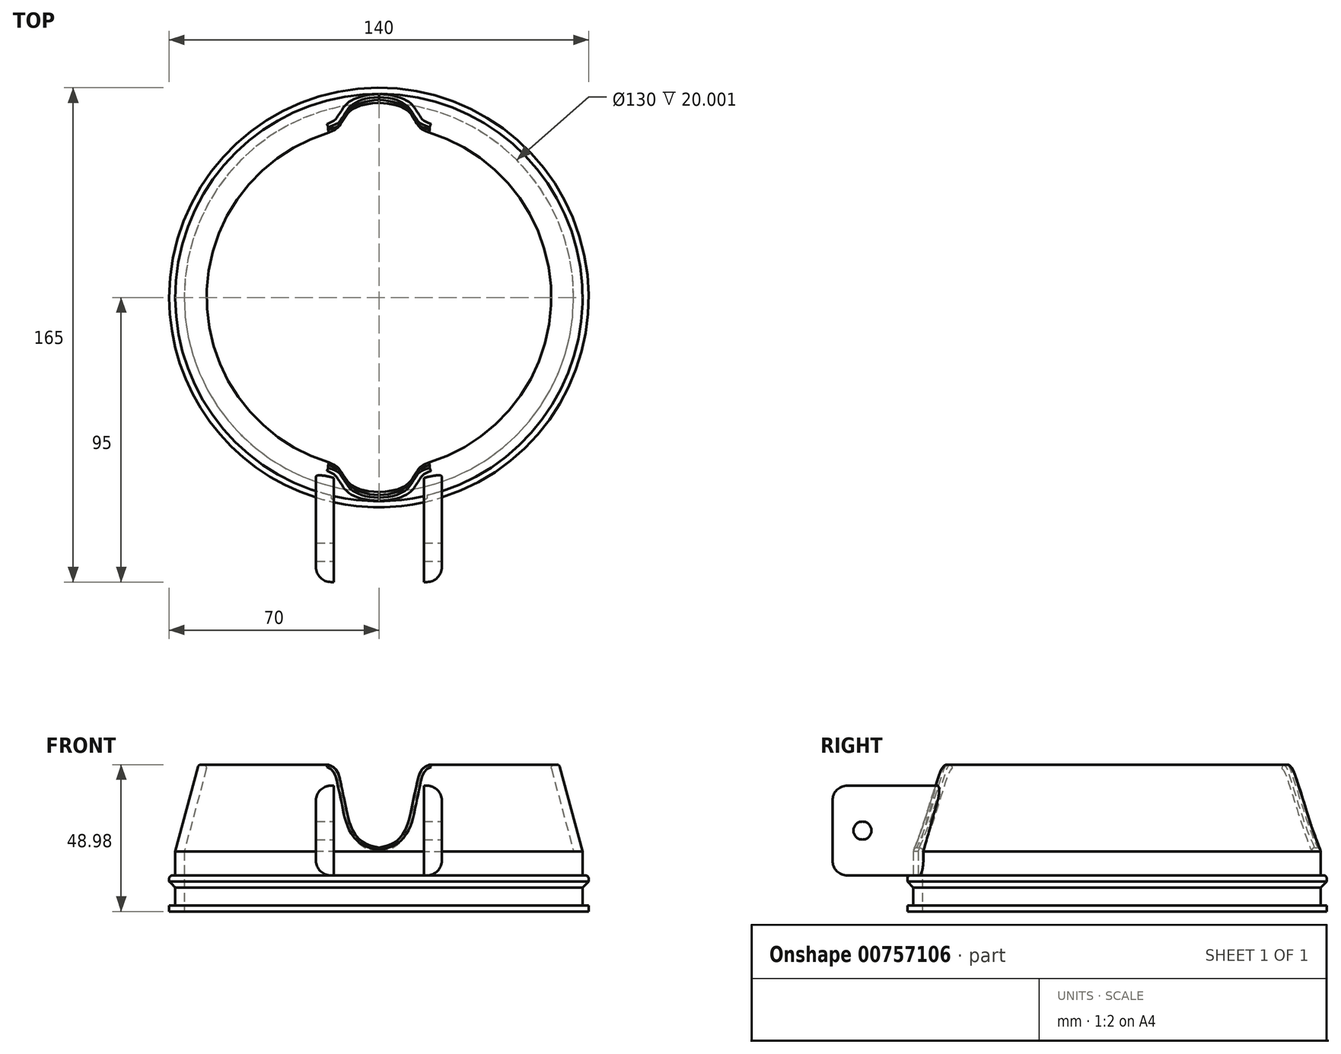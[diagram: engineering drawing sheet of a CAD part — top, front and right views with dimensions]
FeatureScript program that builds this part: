
annotation { "Feature Type Name" : "Feature", "Feature Type Description" : "" }
export const myFeature = defineFeature(function(context is Context, id is Id, definition is map)
    precondition{}
    {
        {
            var Q0;
            Q0=qCreatedBy(makeId("Front.planeOp"),FACE);
            var sketch = newSketch(context, id + "F0", { "sketchPlane" : qUnion([Q0])});
            skLineSegment(sketch, "E0.top", {"start": v(-68, 20) * mm, "end": v(-65, 20) * mm});
            skLineSegment(sketch, "E0.left", {"start": v(-68, 0) * mm, "end": v(-68, 20) * mm});
            skLineSegment(sketch, "E0.right", {"start": v(-65, 0) * mm, "end": v(-65, 20) * mm});
            skLineSegment(sketch, "E1", {"start": v(-68, 20) * mm, "end": v(-60.24, 48.98) * mm});
            skLineSegment(sketch, "E2", {"start": v(-57.24, 48.98) * mm, "end": v(-65, 20) * mm});
            skPoint(sketch, "E3.visualSharp", {"position": v(-68, 0) * mm});
            skPoint(sketch, "E4.visualSharp", {"position": v(-65, 0) * mm});
            skLineSegment(sketch, "E5", {"start": v(-68, 12) * mm, "end": v(-69, 12) * mm});
            skLineSegment(sketch, "E6", {"start": v(-70, 11) * mm, "end": v(-70, 10) * mm});
            skLineSegment(sketch, "E7", {"start": v(-70, 10) * mm, "end": v(-68, 8) * mm});
            skLineSegment(sketch, "E8", {"start": v(-68, 2) * mm, "end": v(-70, 2) * mm});
            skLineSegment(sketch, "E9", {"start": v(-70, 2) * mm, "end": v(-70, 0) * mm});
            skLineSegment(sketch, "E10", {"start": v(-70, 0) * mm, "end": v(-68, 0) * mm});
            skPoint(sketch, "E11.visualSharp", {"position": v(-70, 12) * mm});
            skArc(sketch, "E11.filletArc", {"start": v(-69, 12) * mm, "mid": v(-69.7, 11.7) * mm, "end": v(-70, 11) * mm});
            skLineSegment(sketch, "E12", {"start": v(0, 0) * mm, "end": v(0, 37.2) * mm, "construction": true});
            skLineSegment(sketch, "E13", {"start": v(-60.24, 48.98) * mm, "end": v(-57.24, 48.98) * mm});
            skLineSegment(sketch, "E14", {"start": v(-68, 0) * mm, "end": v(-65, 0) * mm});
            skSolve(sketch);
        }
        {
            var Q0;
            Q0=makeQuery(id+"F0.imprint","IMPRINT",FACE,{"disambiguationData":[TD([[makeQuery(id+"F0.imprint","IMPRINT",EDGE,{"derivedFrom":sQuery(id+"F0.wireOp",EDGE,"E0.bottom")}),1.0]])]});
            var Q1;
            {var subQ0=sQuery(id+"F0.wireOp",EDGE,"E0.top");Q1=makeQuery(id+"F0.imprint","IMPRINT",FACE,{"disambiguationData":[TD([[makeQuery(id+"F0.imprint","IMPRINT",EDGE,{"derivedFrom":subQ0}),1.0]])]});}
            var Q2;
            Q2=makeQuery(id+"F0.imprint","IMPRINT",FACE,{"disambiguationData":[TD([[makeQuery(id+"F0.imprint","IMPRINT",EDGE,{"derivedFrom":sQuery(id+"F0.wireOp",EDGE,"ip61VsO4-G4QX-MuCQ-3TD0-dqhbcXr0CBei")}),1.0]])]});
            var Q3;
            {var subQ1=sQuery(id+"F0.wireOp",EDGE,"E5");Q3=makeQuery(id+"F0.imprint","IMPRINT",FACE,{"disambiguationData":[TD([[makeQuery(id+"F0.imprint","IMPRINT",EDGE,{"derivedFrom":subQ1}),1.0]])]});}
            var Q4;
            {var subQ0=sQuery(id+"F0.wireOp",EDGE,"E8");Q4=makeQuery(id+"F0.imprint","IMPRINT",FACE,{"disambiguationData":[TD([[makeQuery(id+"F0.imprint","IMPRINT",EDGE,{"derivedFrom":subQ0}),1.0]])]});}
            var Q5;
            {var subQ5=sQuery(id+"F0.wireOp",EDGE,"E0.top");Q5=makeQuery(id+"F0.imprint","IMPRINT",FACE,{"disambiguationData":[TD([[makeQuery(id+"F0.imprint","IMPRINT",EDGE,{"derivedFrom":subQ5}),-1.0]])]});}
            var Q6;
            Q6=sQuery(id+"F0.wireOp",EDGE,"E12");
            revolve(context, id + "F1", {"surfaceOperationType" : NewSurfaceOperationType.NEW, "entities" : qUnion([Q0, Q1, Q2, Q3, Q4, Q5]), "axis" : qUnion([Q6]), "revolveType" : RevolveType.FULL});
        }
        {
            var Q0;
            Q0=qCreatedBy(makeId("Front.planeOp"),FACE);
            var sketch = newSketch(context, id + "F2", { "sketchPlane" : qUnion([Q0])});
            skFitSpline(sketch, "E15", {"points": [v(21.47, 49.66) * mm, v(17.18, 49.05) * mm, v(14.22, 47.2) * mm, v(12.69, 42.71) * mm, v(11.26, 35.97) * mm, v(9.52, 28.93) * mm, v(5.64, 23.3) * mm, v(0, 21.26) * mm], "startDerivative": vector(-35.25, -2.77) * mm, "endDerivative": vector(-40.6, -8.65) * mm});
            skFitSpline(sketch, "E16.MirrorCS", {"points": [v(-21.47, 49.66) * mm, v(-17.18, 49.05) * mm, v(-14.22, 47.2) * mm, v(-12.69, 42.71) * mm, v(-11.26, 35.97) * mm, v(-9.52, 28.93) * mm, v(-5.64, 23.3) * mm, v(0, 21.26) * mm], "startDerivative": vector(35.25, -2.77) * mm, "endDerivative": vector(40.6, -8.65) * mm});
            skLineSegment(sketch, "E17", {"start": v(21.47, 49.66) * mm, "end": v(21.47, 54.46) * mm});
            skLineSegment(sketch, "E18", {"start": v(21.47, 54.46) * mm, "end": v(-21.12, 54.46) * mm});
            skLineSegment(sketch, "E19", {"start": v(-21.12, 54.46) * mm, "end": v(-21.47, 49.66) * mm});
            skSolve(sketch);
        }
        {
            var Q0;
            Q0 = qSketchRegion(id + "F2", true);
            extrude(context, id + "F3", {"entities" : qUnion([Q0]), "operationType" : NewBodyOperationType.REMOVE, "endBound" : BoundingType.SYMMETRIC, "depth" : 200 * mm, "offsetDistance" : 25 * mm});
        }
        {
            var Q0;
            Q0=qCreatedBy(makeId("Front.planeOp"),FACE);
            cPlane(context, id + "F4", {"entities" : qUnion([Q0]), "cplaneType" : CPlaneType.OFFSET, "offset" : 95 * mm, "width" : 150 * mm, "height" : 150 * mm});
        }
        {
            var Q0;
            Q0=qCreatedBy(id+"F4.planeOp",FACE);
            var sketch = newSketch(context, id + "F5", { "sketchPlane" : qUnion([Q0])});
            skLineSegment(sketch, "E20.bottom", {"start": v(-21, 42) * mm, "end": v(-15, 42) * mm});
            skLineSegment(sketch, "E20.top", {"start": v(-21, 12) * mm, "end": v(-15, 12) * mm});
            skLineSegment(sketch, "E20.left", {"start": v(-21, 42) * mm, "end": v(-21, 12) * mm});
            skLineSegment(sketch, "E20.right", {"start": v(-15, 42) * mm, "end": v(-15, 12) * mm});
            skLineSegment(sketch, "E21.MirrorCS", {"start": v(15, 42) * mm, "end": v(15, 12) * mm});
            skLineSegment(sketch, "E22.MirrorCS", {"start": v(21, 42) * mm, "end": v(15, 42) * mm});
            skLineSegment(sketch, "E23.MirrorCS", {"start": v(21, 12) * mm, "end": v(15, 12) * mm});
            skLineSegment(sketch, "E24.MirrorCS", {"start": v(21, 42) * mm, "end": v(21, 12) * mm});
            skSolve(sketch);
        }
        {
            var Q0;
            Q0 = qSketchRegion(id + "F5", true);
            extrude(context, id + "F6", {"entities" : qUnion([Q0]), "operationType" : NewBodyOperationType.ADD, "endBound" : BoundingType.UP_TO_NEXT, "oppositeDirection" : true, "depth" : 25 * mm, "offsetDistance" : 25 * mm});
        }
        {
            var Q0;
            Q0=makeQuery(id+"F6.opExtrude","CAP_EDGE",EDGE,{"disambiguationData":[OSD([sQuery(id+"F5.wireOp",EDGE,"E20.bottom")])],"isStart":true});
            var Q1;
            Q1=makeQuery(id+"F6.opExtrude","CAP_EDGE",EDGE,{"disambiguationData":[OSD([sQuery(id+"F5.wireOp",EDGE,"E20.top")])],"isStart":true});
            var Q2;
            Q2=makeQuery(id+"F6.opExtrude","CAP_EDGE",EDGE,{"disambiguationData":[OSD([sQuery(id+"F5.wireOp",EDGE,"E22.MirrorCS")])],"isStart":true});
            var Q3;
            Q3=makeQuery(id+"F6.opExtrude","CAP_EDGE",EDGE,{"disambiguationData":[OSD([sQuery(id+"F5.wireOp",EDGE,"E23.MirrorCS")])],"isStart":true});
            fillet(context, id + "F7", {"entities" : qUnion([Q0, Q1, Q2, Q3]), "radius" : 5 * mm, "tangentPropagation" : true, "allowEdgeOverflow" : false});
        }
        {
            var Q0;
            Q0=makeQuery(id+"F6.opExtrude","SWEPT_FACE",FACE,{"disambiguationData":[OSD([sQuery(id+"F5.wireOp",EDGE,"E24.MirrorCS")])]});
            var sketch = newSketch(context, id + "F8", { "sketchPlane" : qUnion([Q0])});
            skCircle(sketch, "E25", {"center": v(-85, 27) * mm, "radius": 3 * mm});
            skPoint(sketch, "E25.centerSnap0", {"position": v(-95, 27) * mm});
            skSolve(sketch);
        }
        {
            var Q0;
            Q0=makeQuery(id+"F8.imprint","IMPRINT",FACE,{"disambiguationData":[TD([[makeQuery(id+"F8.imprint","IMPRINT",EDGE,{"derivedFrom":sQuery(id+"F8.wireOp",EDGE,"E25")}),1.0]])]});
            extrude(context, id + "F9", {"entities" : qUnion([Q0]), "operationType" : NewBodyOperationType.REMOVE, "endBound" : BoundingType.THROUGH_ALL, "oppositeDirection" : true, "depth" : 25 * mm, "offsetDistance" : 25 * mm});
        }
        {
            var Q0;
            Q0=makeQuery(id+"F6.opExtrude","CAP_EDGE",EDGE,{"disambiguationData":[OSD([sQuery(id+"F5.wireOp",EDGE,"E20.left")])],"isStart":true});
            var Q1;
            Q1=makeQuery(id+"F6.opExtrude","CAP_EDGE",EDGE,{"disambiguationData":[OSD([sQuery(id+"F5.wireOp",EDGE,"E24.MirrorCS")])],"isStart":true});
            fillet(context, id + "F10", {"entities" : qUnion([Q0, Q1]), "radius" : 5 * mm, "tangentPropagation" : true, "allowEdgeOverflow" : false});
        }
        {
            var Q0;
            {var subQ0=sQuery(id+"F0.wireOp",EDGE,"E2");var subQ2=sQuery(id+"F0.wireOp",EDGE,"E13");var subQ4=makeQuery(id+"F3.opExtrude","SWEPT_FACE",FACE,{"disambiguationData":[OSD([sQuery(id+"F2.wireOp",EDGE,"E16.MirrorCS")])]});Q0=makeQuery(id+"Fq1PH19bnDTYdRj_1.1.F3.boolean.opBoolean","SPLIT",EDGE,{"disambiguationData":[TD([makeQuery(id+"F3.boolean.opBoolean","COPY",FACE,{"disambiguationData":[OD(0.0)],"derivedFrom":subQ4})])],"derivedFrom":makeQuery(id+"F3.boolean.opBoolean","SPLIT",EDGE,{"disambiguationData":[TD([subQ4])],"derivedFrom":makeQuery(id+"F1.opRevolve","SWEPT_EDGE",EDGE,{"disambiguationData":[OSD([subQ0,subQ2])]})})});}
            var Q1;
            Q1=makeQuery(id+"F3.boolean.opBoolean","INTERSECT",EDGE,{"disambiguationData":[OD(0.0)],"derivedFrom":[makeQuery(id+"F1.opRevolve","SWEPT_FACE",FACE,{"disambiguationData":[OSD([sQuery(id+"F0.wireOp",EDGE,"E2")])]}),makeQuery(id+"F3.opExtrude","SWEPT_FACE",FACE,{"disambiguationData":[OSD([sQuery(id+"F2.wireOp",EDGE,"E16.MirrorCS")])]})]});
            var Q2;
            Q2=makeQuery(id+"F3.boolean.opBoolean","INTERSECT",EDGE,{"disambiguationData":[OD(0.0)],"derivedFrom":[makeQuery(id+"F1.opRevolve","SWEPT_FACE",FACE,{"disambiguationData":[OSD([sQuery(id+"F0.wireOp",EDGE,"E2")])]}),makeQuery(id+"F3.opExtrude","SWEPT_FACE",FACE,{"disambiguationData":[OSD([sQuery(id+"F2.wireOp",EDGE,"E15")])]})]});
            var Q3;
            {var subQ0=sQuery(id+"F0.wireOp",EDGE,"E2");var subQ2=sQuery(id+"F2.wireOp",EDGE,"E15");var subQ3=makeQuery(id+"F3.opExtrude","SWEPT_FACE",FACE,{"disambiguationData":[OSD([subQ2])]});var subQ4=makeQuery(id+"F3.boolean.opBoolean","COPY",FACE,{"disambiguationData":[OD(0.0)],"derivedFrom":subQ3});var subQ5=sQuery(id+"F0.wireOp",EDGE,"E13");Q3=makeQuery(id+"Fq1PH19bnDTYdRj_1.3.F3.boolean.opBoolean","SPLIT",EDGE,{"disambiguationData":[TD([subQ4])],"derivedFrom":makeQuery(id+"Fq1PH19bnDTYdRj_1.2.F3.boolean.opBoolean","SPLIT",EDGE,{"disambiguationData":[TD([subQ4])],"derivedFrom":makeQuery(id+"Fq1PH19bnDTYdRj_1.1.F3.boolean.opBoolean","SPLIT",EDGE,{"disambiguationData":[TD([subQ4])],"derivedFrom":makeQuery(id+"F3.boolean.opBoolean","SPLIT",EDGE,{"disambiguationData":[TD([subQ3])],"derivedFrom":makeQuery(id+"F1.opRevolve","SWEPT_EDGE",EDGE,{"disambiguationData":[OSD([subQ0,subQ5])]})})})})});}
            var Q4;
            Q4=makeQuery(id+"Fq1PH19bnDTYdRj_1.3.F3.boolean.opBoolean","INTERSECT",EDGE,{"disambiguationData":[OD(1.0)],"derivedFrom":[makeQuery(id+"F1.opRevolve","SWEPT_FACE",FACE,{"disambiguationData":[OSD([sQuery(id+"F0.wireOp",EDGE,"E2")])]}),makeQuery(id+"Fq1PH19bnDTYdRj_1.3.F3.opExtrude","SWEPT_FACE",FACE,{"disambiguationData":[OSD([sQuery(id+"F2.wireOp",EDGE,"E15")])]})]});
            var Q5;
            Q5=makeQuery(id+"Fq1PH19bnDTYdRj_1.3.F3.boolean.opBoolean","INTERSECT",EDGE,{"disambiguationData":[OD(1.0)],"derivedFrom":[makeQuery(id+"F1.opRevolve","SWEPT_FACE",FACE,{"disambiguationData":[OSD([sQuery(id+"F0.wireOp",EDGE,"E2")])]}),makeQuery(id+"Fq1PH19bnDTYdRj_1.3.F3.opExtrude","SWEPT_FACE",FACE,{"disambiguationData":[OSD([sQuery(id+"F2.wireOp",EDGE,"E16.MirrorCS")])]})]});
            var Q6;
            {var subQ0=sQuery(id+"F0.wireOp",EDGE,"E2");var subQ2=sQuery(id+"F0.wireOp",EDGE,"E13");var subQ4=sQuery(id+"F2.wireOp",EDGE,"E15");var subQ5=makeQuery(id+"Fq1PH19bnDTYdRj_1.2.F3.opExtrude","SWEPT_FACE",FACE,{"disambiguationData":[OSD([subQ4])]});var subQ6=makeQuery(id+"F3.opExtrude","SWEPT_FACE",FACE,{"disambiguationData":[OSD([subQ4])]});var subQ7=makeQuery(id+"F3.boolean.opBoolean","COPY",FACE,{"disambiguationData":[OD(0.0)],"derivedFrom":subQ6});Q6=makeQuery(id+"Fq1PH19bnDTYdRj_1.3.F3.boolean.opBoolean","SPLIT",EDGE,{"disambiguationData":[TD([makeQuery(id+"Fq1PH19bnDTYdRj_1.2.F3.boolean.opBoolean","COPY",FACE,{"disambiguationData":[OD(1.0)],"derivedFrom":subQ5})])],"derivedFrom":makeQuery(id+"Fq1PH19bnDTYdRj_1.2.F3.boolean.opBoolean","SPLIT",EDGE,{"disambiguationData":[TD([subQ7])],"derivedFrom":makeQuery(id+"Fq1PH19bnDTYdRj_1.1.F3.boolean.opBoolean","SPLIT",EDGE,{"disambiguationData":[TD([subQ7])],"derivedFrom":makeQuery(id+"F3.boolean.opBoolean","SPLIT",EDGE,{"disambiguationData":[TD([subQ6])],"derivedFrom":makeQuery(id+"F1.opRevolve","SWEPT_EDGE",EDGE,{"disambiguationData":[OSD([subQ0,subQ2])]})})})})});}
            var Q7;
            Q7=makeQuery(id+"Fq1PH19bnDTYdRj_1.2.F3.boolean.opBoolean","INTERSECT",EDGE,{"disambiguationData":[OD(1.0)],"derivedFrom":[makeQuery(id+"F1.opRevolve","SWEPT_FACE",FACE,{"disambiguationData":[OSD([sQuery(id+"F0.wireOp",EDGE,"E2")])]}),makeQuery(id+"Fq1PH19bnDTYdRj_1.2.F3.opExtrude","SWEPT_FACE",FACE,{"disambiguationData":[OSD([sQuery(id+"F2.wireOp",EDGE,"E15")])]})]});
            var Q8;
            Q8=makeQuery(id+"Fq1PH19bnDTYdRj_1.2.F3.boolean.opBoolean","INTERSECT",EDGE,{"disambiguationData":[OD(1.0)],"derivedFrom":[makeQuery(id+"F1.opRevolve","SWEPT_FACE",FACE,{"disambiguationData":[OSD([sQuery(id+"F0.wireOp",EDGE,"E2")])]}),makeQuery(id+"Fq1PH19bnDTYdRj_1.2.F3.opExtrude","SWEPT_FACE",FACE,{"disambiguationData":[OSD([sQuery(id+"F2.wireOp",EDGE,"E16.MirrorCS")])]})]});
            var Q9;
            {var subQ0=sQuery(id+"F0.wireOp",EDGE,"E2");var subQ2=sQuery(id+"F2.wireOp",EDGE,"E15");var subQ3=makeQuery(id+"Fq1PH19bnDTYdRj_1.1.F3.opExtrude","SWEPT_FACE",FACE,{"disambiguationData":[OSD([subQ2])]});var subQ4=sQuery(id+"F0.wireOp",EDGE,"E13");var subQ6=makeQuery(id+"F3.opExtrude","SWEPT_FACE",FACE,{"disambiguationData":[OSD([subQ2])]});Q9=makeQuery(id+"Fq1PH19bnDTYdRj_1.2.F3.boolean.opBoolean","SPLIT",EDGE,{"disambiguationData":[TD([makeQuery(id+"Fq1PH19bnDTYdRj_1.1.F3.boolean.opBoolean","COPY",FACE,{"disambiguationData":[OD(1.0)],"derivedFrom":subQ3})])],"derivedFrom":makeQuery(id+"Fq1PH19bnDTYdRj_1.1.F3.boolean.opBoolean","SPLIT",EDGE,{"disambiguationData":[TD([makeQuery(id+"F3.boolean.opBoolean","COPY",FACE,{"disambiguationData":[OD(0.0)],"derivedFrom":subQ6})])],"derivedFrom":makeQuery(id+"F3.boolean.opBoolean","SPLIT",EDGE,{"disambiguationData":[TD([subQ6])],"derivedFrom":makeQuery(id+"F1.opRevolve","SWEPT_EDGE",EDGE,{"disambiguationData":[OSD([subQ0,subQ4])]})})})});}
            var Q10;
            Q10=makeQuery(id+"Fq1PH19bnDTYdRj_1.1.F3.boolean.opBoolean","INTERSECT",EDGE,{"disambiguationData":[OD(1.0)],"derivedFrom":[makeQuery(id+"F1.opRevolve","SWEPT_FACE",FACE,{"disambiguationData":[OSD([sQuery(id+"F0.wireOp",EDGE,"E2")])]}),makeQuery(id+"Fq1PH19bnDTYdRj_1.1.F3.opExtrude","SWEPT_FACE",FACE,{"disambiguationData":[OSD([sQuery(id+"F2.wireOp",EDGE,"E15")])]})]});
            var Q11;
            Q11=makeQuery(id+"Fq1PH19bnDTYdRj_1.1.F3.boolean.opBoolean","INTERSECT",EDGE,{"disambiguationData":[OD(1.0)],"derivedFrom":[makeQuery(id+"F1.opRevolve","SWEPT_FACE",FACE,{"disambiguationData":[OSD([sQuery(id+"F0.wireOp",EDGE,"E2")])]}),makeQuery(id+"Fq1PH19bnDTYdRj_1.1.F3.opExtrude","SWEPT_FACE",FACE,{"disambiguationData":[OSD([sQuery(id+"F2.wireOp",EDGE,"E16.MirrorCS")])]})]});
            var Q12;
            {var subQ0=sQuery(id+"F0.wireOp",EDGE,"E2");var subQ2=sQuery(id+"F0.wireOp",EDGE,"E13");var subQ4=makeQuery(id+"F3.opExtrude","SWEPT_FACE",FACE,{"disambiguationData":[OSD([sQuery(id+"F2.wireOp",EDGE,"E15")])]});Q12=makeQuery(id+"Fq1PH19bnDTYdRj_1.1.F3.boolean.opBoolean","SPLIT",EDGE,{"disambiguationData":[TD([makeQuery(id+"F3.boolean.opBoolean","COPY",FACE,{"disambiguationData":[OD(1.0)],"derivedFrom":subQ4})])],"derivedFrom":makeQuery(id+"F3.boolean.opBoolean","SPLIT",EDGE,{"disambiguationData":[TD([subQ4])],"derivedFrom":makeQuery(id+"F1.opRevolve","SWEPT_EDGE",EDGE,{"disambiguationData":[OSD([subQ0,subQ2])]})})});}
            var Q13;
            Q13=makeQuery(id+"F3.boolean.opBoolean","INTERSECT",EDGE,{"disambiguationData":[OD(1.0)],"derivedFrom":[makeQuery(id+"F1.opRevolve","SWEPT_FACE",FACE,{"disambiguationData":[OSD([sQuery(id+"F0.wireOp",EDGE,"E2")])]}),makeQuery(id+"F3.opExtrude","SWEPT_FACE",FACE,{"disambiguationData":[OSD([sQuery(id+"F2.wireOp",EDGE,"E15")])]})]});
            var Q14;
            Q14=makeQuery(id+"F3.boolean.opBoolean","INTERSECT",EDGE,{"disambiguationData":[OD(1.0)],"derivedFrom":[makeQuery(id+"F1.opRevolve","SWEPT_FACE",FACE,{"disambiguationData":[OSD([sQuery(id+"F0.wireOp",EDGE,"E2")])]}),makeQuery(id+"F3.opExtrude","SWEPT_FACE",FACE,{"disambiguationData":[OSD([sQuery(id+"F2.wireOp",EDGE,"E16.MirrorCS")])]})]});
            var Q15;
            {var subQ0=sQuery(id+"F0.wireOp",EDGE,"E2");var subQ2=sQuery(id+"F0.wireOp",EDGE,"E13");var subQ4=sQuery(id+"F2.wireOp",EDGE,"E16.MirrorCS");var subQ5=makeQuery(id+"F3.opExtrude","SWEPT_FACE",FACE,{"disambiguationData":[OSD([subQ4])]});var subQ6=makeQuery(id+"F3.boolean.opBoolean","COPY",FACE,{"disambiguationData":[OD(1.0)],"derivedFrom":subQ5});Q15=makeQuery(id+"Fq1PH19bnDTYdRj_1.3.F3.boolean.opBoolean","SPLIT",EDGE,{"disambiguationData":[TD([subQ6])],"derivedFrom":makeQuery(id+"Fq1PH19bnDTYdRj_1.2.F3.boolean.opBoolean","SPLIT",EDGE,{"disambiguationData":[TD([subQ6])],"derivedFrom":makeQuery(id+"Fq1PH19bnDTYdRj_1.1.F3.boolean.opBoolean","SPLIT",EDGE,{"disambiguationData":[TD([subQ6])],"derivedFrom":makeQuery(id+"F3.boolean.opBoolean","SPLIT",EDGE,{"disambiguationData":[TD([subQ5])],"derivedFrom":makeQuery(id+"F1.opRevolve","SWEPT_EDGE",EDGE,{"disambiguationData":[OSD([subQ0,subQ2])]})})})})});}
            var Q16;
            Q16=makeQuery(id+"Fq1PH19bnDTYdRj_1.3.F3.boolean.opBoolean","INTERSECT",EDGE,{"disambiguationData":[OD(0.0)],"derivedFrom":[makeQuery(id+"F1.opRevolve","SWEPT_FACE",FACE,{"disambiguationData":[OSD([sQuery(id+"F0.wireOp",EDGE,"E2")])]}),makeQuery(id+"Fq1PH19bnDTYdRj_1.3.F3.opExtrude","SWEPT_FACE",FACE,{"disambiguationData":[OSD([sQuery(id+"F2.wireOp",EDGE,"E16.MirrorCS")])]})]});
            var Q17;
            Q17=makeQuery(id+"Fq1PH19bnDTYdRj_1.3.F3.boolean.opBoolean","INTERSECT",EDGE,{"disambiguationData":[OD(0.0)],"derivedFrom":[makeQuery(id+"F1.opRevolve","SWEPT_FACE",FACE,{"disambiguationData":[OSD([sQuery(id+"F0.wireOp",EDGE,"E2")])]}),makeQuery(id+"Fq1PH19bnDTYdRj_1.3.F3.opExtrude","SWEPT_FACE",FACE,{"disambiguationData":[OSD([sQuery(id+"F2.wireOp",EDGE,"E15")])]})]});
            var Q18;
            {var subQ0=sQuery(id+"F0.wireOp",EDGE,"E2");var subQ2=sQuery(id+"F0.wireOp",EDGE,"E13");var subQ4=sQuery(id+"F2.wireOp",EDGE,"E16.MirrorCS");var subQ5=makeQuery(id+"Fq1PH19bnDTYdRj_1.2.F3.opExtrude","SWEPT_FACE",FACE,{"disambiguationData":[OSD([subQ4])]});var subQ6=makeQuery(id+"F3.opExtrude","SWEPT_FACE",FACE,{"disambiguationData":[OSD([subQ4])]});var subQ7=makeQuery(id+"F3.boolean.opBoolean","COPY",FACE,{"disambiguationData":[OD(1.0)],"derivedFrom":subQ6});Q18=makeQuery(id+"Fq1PH19bnDTYdRj_1.3.F3.boolean.opBoolean","SPLIT",EDGE,{"disambiguationData":[TD([makeQuery(id+"Fq1PH19bnDTYdRj_1.2.F3.boolean.opBoolean","COPY",FACE,{"disambiguationData":[OD(0.0)],"derivedFrom":subQ5})])],"derivedFrom":makeQuery(id+"Fq1PH19bnDTYdRj_1.2.F3.boolean.opBoolean","SPLIT",EDGE,{"disambiguationData":[TD([subQ7])],"derivedFrom":makeQuery(id+"Fq1PH19bnDTYdRj_1.1.F3.boolean.opBoolean","SPLIT",EDGE,{"disambiguationData":[TD([subQ7])],"derivedFrom":makeQuery(id+"F3.boolean.opBoolean","SPLIT",EDGE,{"disambiguationData":[TD([subQ6])],"derivedFrom":makeQuery(id+"F1.opRevolve","SWEPT_EDGE",EDGE,{"disambiguationData":[OSD([subQ0,subQ2])]})})})})});}
            var Q19;
            Q19=makeQuery(id+"Fq1PH19bnDTYdRj_1.2.F3.boolean.opBoolean","INTERSECT",EDGE,{"disambiguationData":[OD(0.0)],"derivedFrom":[makeQuery(id+"F1.opRevolve","SWEPT_FACE",FACE,{"disambiguationData":[OSD([sQuery(id+"F0.wireOp",EDGE,"E2")])]}),makeQuery(id+"Fq1PH19bnDTYdRj_1.2.F3.opExtrude","SWEPT_FACE",FACE,{"disambiguationData":[OSD([sQuery(id+"F2.wireOp",EDGE,"E16.MirrorCS")])]})]});
            var Q20;
            Q20=makeQuery(id+"Fq1PH19bnDTYdRj_1.2.F3.boolean.opBoolean","INTERSECT",EDGE,{"disambiguationData":[OD(0.0)],"derivedFrom":[makeQuery(id+"F1.opRevolve","SWEPT_FACE",FACE,{"disambiguationData":[OSD([sQuery(id+"F0.wireOp",EDGE,"E2")])]}),makeQuery(id+"Fq1PH19bnDTYdRj_1.2.F3.opExtrude","SWEPT_FACE",FACE,{"disambiguationData":[OSD([sQuery(id+"F2.wireOp",EDGE,"E15")])]})]});
            var Q21;
            {var subQ0=sQuery(id+"F0.wireOp",EDGE,"E2");var subQ2=sQuery(id+"F0.wireOp",EDGE,"E13");var subQ4=sQuery(id+"F2.wireOp",EDGE,"E16.MirrorCS");var subQ5=makeQuery(id+"Fq1PH19bnDTYdRj_1.1.F3.opExtrude","SWEPT_FACE",FACE,{"disambiguationData":[OSD([subQ4])]});var subQ6=makeQuery(id+"F3.opExtrude","SWEPT_FACE",FACE,{"disambiguationData":[OSD([subQ4])]});Q21=makeQuery(id+"Fq1PH19bnDTYdRj_1.2.F3.boolean.opBoolean","SPLIT",EDGE,{"disambiguationData":[TD([makeQuery(id+"Fq1PH19bnDTYdRj_1.1.F3.boolean.opBoolean","COPY",FACE,{"disambiguationData":[OD(0.0)],"derivedFrom":subQ5})])],"derivedFrom":makeQuery(id+"Fq1PH19bnDTYdRj_1.1.F3.boolean.opBoolean","SPLIT",EDGE,{"disambiguationData":[TD([makeQuery(id+"F3.boolean.opBoolean","COPY",FACE,{"disambiguationData":[OD(1.0)],"derivedFrom":subQ6})])],"derivedFrom":makeQuery(id+"F3.boolean.opBoolean","SPLIT",EDGE,{"disambiguationData":[TD([subQ6])],"derivedFrom":makeQuery(id+"F1.opRevolve","SWEPT_EDGE",EDGE,{"disambiguationData":[OSD([subQ0,subQ2])]})})})});}
            var Q22;
            Q22=makeQuery(id+"Fq1PH19bnDTYdRj_1.1.F3.boolean.opBoolean","INTERSECT",EDGE,{"disambiguationData":[OD(0.0)],"derivedFrom":[makeQuery(id+"F1.opRevolve","SWEPT_FACE",FACE,{"disambiguationData":[OSD([sQuery(id+"F0.wireOp",EDGE,"E2")])]}),makeQuery(id+"Fq1PH19bnDTYdRj_1.1.F3.opExtrude","SWEPT_FACE",FACE,{"disambiguationData":[OSD([sQuery(id+"F2.wireOp",EDGE,"E16.MirrorCS")])]})]});
            var Q23;
            Q23=makeQuery(id+"Fq1PH19bnDTYdRj_1.1.F3.boolean.opBoolean","INTERSECT",EDGE,{"disambiguationData":[OD(0.0)],"derivedFrom":[makeQuery(id+"F1.opRevolve","SWEPT_FACE",FACE,{"disambiguationData":[OSD([sQuery(id+"F0.wireOp",EDGE,"E2")])]}),makeQuery(id+"Fq1PH19bnDTYdRj_1.1.F3.opExtrude","SWEPT_FACE",FACE,{"disambiguationData":[OSD([sQuery(id+"F2.wireOp",EDGE,"E15")])]})]});
            fillet(context, id + "F11", {"entities" : qUnion([Q0, Q1, Q2, Q3, Q4, Q5, Q6, Q7, Q8, Q9, Q10, Q11, Q12, Q13, Q14, Q15, Q16, Q17, Q18, Q19, Q20, Q21, Q22, Q23]), "radius" : 1 * mm, "tangentPropagation" : true, "allowEdgeOverflow" : false});
        }
        {
            var Q0;
            {var subQ0=sQuery(id+"F0.wireOp",EDGE,"E1");var subQ2=sQuery(id+"F0.wireOp",EDGE,"E13");var subQ4=sQuery(id+"F2.wireOp",EDGE,"E15");var subQ5=makeQuery(id+"Fq1PH19bnDTYdRj_1.1.F3.opExtrude","SWEPT_FACE",FACE,{"disambiguationData":[OSD([subQ4])]});var subQ6=makeQuery(id+"F3.opExtrude","SWEPT_FACE",FACE,{"disambiguationData":[OSD([subQ4])]});Q0=makeQuery(id+"Fq1PH19bnDTYdRj_1.2.F3.boolean.opBoolean","SPLIT",EDGE,{"disambiguationData":[TD([makeQuery(id+"Fq1PH19bnDTYdRj_1.1.F3.boolean.opBoolean","COPY",FACE,{"disambiguationData":[OD(1.0)],"derivedFrom":subQ5})])],"derivedFrom":makeQuery(id+"Fq1PH19bnDTYdRj_1.1.F3.boolean.opBoolean","SPLIT",EDGE,{"disambiguationData":[TD([makeQuery(id+"F3.boolean.opBoolean","COPY",FACE,{"disambiguationData":[OD(0.0)],"derivedFrom":subQ6})])],"derivedFrom":makeQuery(id+"F3.boolean.opBoolean","SPLIT",EDGE,{"disambiguationData":[TD([subQ6])],"derivedFrom":makeQuery(id+"F1.opRevolve","SWEPT_EDGE",EDGE,{"disambiguationData":[OSD([subQ0,subQ2])]})})})});}
            var Q1;
            Q1=makeQuery(id+"Fq1PH19bnDTYdRj_1.2.F3.boolean.opBoolean","INTERSECT",EDGE,{"disambiguationData":[OD(1.0)],"derivedFrom":[makeQuery(id+"F1.opRevolve","SWEPT_FACE",FACE,{"disambiguationData":[OSD([sQuery(id+"F0.wireOp",EDGE,"E1")])]}),makeQuery(id+"Fq1PH19bnDTYdRj_1.2.F3.opExtrude","SWEPT_FACE",FACE,{"disambiguationData":[OSD([sQuery(id+"F2.wireOp",EDGE,"E16.MirrorCS")])]})]});
            var Q2;
            Q2=makeQuery(id+"Fq1PH19bnDTYdRj_1.2.F3.boolean.opBoolean","INTERSECT",EDGE,{"disambiguationData":[OD(1.0)],"derivedFrom":[makeQuery(id+"F1.opRevolve","SWEPT_FACE",FACE,{"disambiguationData":[OSD([sQuery(id+"F0.wireOp",EDGE,"E1")])]}),makeQuery(id+"Fq1PH19bnDTYdRj_1.2.F3.opExtrude","SWEPT_FACE",FACE,{"disambiguationData":[OSD([sQuery(id+"F2.wireOp",EDGE,"E15")])]})]});
            var Q3;
            Q3=makeQuery(id+"Fq1PH19bnDTYdRj_1.3.F3.boolean.opBoolean","INTERSECT",EDGE,{"disambiguationData":[OD(1.0)],"derivedFrom":[makeQuery(id+"F1.opRevolve","SWEPT_FACE",FACE,{"disambiguationData":[OSD([sQuery(id+"F0.wireOp",EDGE,"E1")])]}),makeQuery(id+"Fq1PH19bnDTYdRj_1.3.F3.opExtrude","SWEPT_FACE",FACE,{"disambiguationData":[OSD([sQuery(id+"F2.wireOp",EDGE,"E16.MirrorCS")])]})]});
            var Q4;
            {var subQ0=sQuery(id+"F0.wireOp",EDGE,"E1");var subQ2=sQuery(id+"F0.wireOp",EDGE,"E13");var subQ4=sQuery(id+"F2.wireOp",EDGE,"E15");var subQ5=makeQuery(id+"Fq1PH19bnDTYdRj_1.2.F3.opExtrude","SWEPT_FACE",FACE,{"disambiguationData":[OSD([subQ4])]});var subQ6=makeQuery(id+"F3.opExtrude","SWEPT_FACE",FACE,{"disambiguationData":[OSD([subQ4])]});var subQ7=makeQuery(id+"F3.boolean.opBoolean","COPY",FACE,{"disambiguationData":[OD(0.0)],"derivedFrom":subQ6});Q4=makeQuery(id+"Fq1PH19bnDTYdRj_1.3.F3.boolean.opBoolean","SPLIT",EDGE,{"disambiguationData":[TD([makeQuery(id+"Fq1PH19bnDTYdRj_1.2.F3.boolean.opBoolean","COPY",FACE,{"disambiguationData":[OD(1.0)],"derivedFrom":subQ5})])],"derivedFrom":makeQuery(id+"Fq1PH19bnDTYdRj_1.2.F3.boolean.opBoolean","SPLIT",EDGE,{"disambiguationData":[TD([subQ7])],"derivedFrom":makeQuery(id+"Fq1PH19bnDTYdRj_1.1.F3.boolean.opBoolean","SPLIT",EDGE,{"disambiguationData":[TD([subQ7])],"derivedFrom":makeQuery(id+"F3.boolean.opBoolean","SPLIT",EDGE,{"disambiguationData":[TD([subQ6])],"derivedFrom":makeQuery(id+"F1.opRevolve","SWEPT_EDGE",EDGE,{"disambiguationData":[OSD([subQ0,subQ2])]})})})})});}
            var Q5;
            Q5=makeQuery(id+"Fq1PH19bnDTYdRj_1.3.F3.boolean.opBoolean","INTERSECT",EDGE,{"disambiguationData":[OD(1.0)],"derivedFrom":[makeQuery(id+"F1.opRevolve","SWEPT_FACE",FACE,{"disambiguationData":[OSD([sQuery(id+"F0.wireOp",EDGE,"E1")])]}),makeQuery(id+"Fq1PH19bnDTYdRj_1.3.F3.opExtrude","SWEPT_FACE",FACE,{"disambiguationData":[OSD([sQuery(id+"F2.wireOp",EDGE,"E15")])]})]});
            var Q6;
            Q6=makeQuery(id+"F3.boolean.opBoolean","INTERSECT",EDGE,{"disambiguationData":[OD(0.0)],"derivedFrom":[makeQuery(id+"F1.opRevolve","SWEPT_FACE",FACE,{"disambiguationData":[OSD([sQuery(id+"F0.wireOp",EDGE,"E1")])]}),makeQuery(id+"F3.opExtrude","SWEPT_FACE",FACE,{"disambiguationData":[OSD([sQuery(id+"F2.wireOp",EDGE,"E15")])]})]});
            var Q7;
            {var subQ0=sQuery(id+"F0.wireOp",EDGE,"E1");var subQ2=sQuery(id+"F0.wireOp",EDGE,"E13");var subQ4=sQuery(id+"F2.wireOp",EDGE,"E15");var subQ5=makeQuery(id+"F3.opExtrude","SWEPT_FACE",FACE,{"disambiguationData":[OSD([subQ4])]});var subQ6=makeQuery(id+"F3.boolean.opBoolean","COPY",FACE,{"disambiguationData":[OD(0.0)],"derivedFrom":subQ5});Q7=makeQuery(id+"Fq1PH19bnDTYdRj_1.3.F3.boolean.opBoolean","SPLIT",EDGE,{"disambiguationData":[TD([subQ6])],"derivedFrom":makeQuery(id+"Fq1PH19bnDTYdRj_1.2.F3.boolean.opBoolean","SPLIT",EDGE,{"disambiguationData":[TD([subQ6])],"derivedFrom":makeQuery(id+"Fq1PH19bnDTYdRj_1.1.F3.boolean.opBoolean","SPLIT",EDGE,{"disambiguationData":[TD([subQ6])],"derivedFrom":makeQuery(id+"F3.boolean.opBoolean","SPLIT",EDGE,{"disambiguationData":[TD([subQ5])],"derivedFrom":makeQuery(id+"F1.opRevolve","SWEPT_EDGE",EDGE,{"disambiguationData":[OSD([subQ0,subQ2])]})})})})});}
            var Q8;
            Q8=makeQuery(id+"F3.boolean.opBoolean","INTERSECT",EDGE,{"disambiguationData":[OD(0.0)],"derivedFrom":[makeQuery(id+"F1.opRevolve","SWEPT_FACE",FACE,{"disambiguationData":[OSD([sQuery(id+"F0.wireOp",EDGE,"E1")])]}),makeQuery(id+"F3.opExtrude","SWEPT_FACE",FACE,{"disambiguationData":[OSD([sQuery(id+"F2.wireOp",EDGE,"E16.MirrorCS")])]})]});
            var Q9;
            Q9=makeQuery(id+"Fq1PH19bnDTYdRj_1.1.F3.boolean.opBoolean","INTERSECT",EDGE,{"disambiguationData":[OD(0.0)],"derivedFrom":[makeQuery(id+"F1.opRevolve","SWEPT_FACE",FACE,{"disambiguationData":[OSD([sQuery(id+"F0.wireOp",EDGE,"E1")])]}),makeQuery(id+"Fq1PH19bnDTYdRj_1.1.F3.opExtrude","SWEPT_FACE",FACE,{"disambiguationData":[OSD([sQuery(id+"F2.wireOp",EDGE,"E15")])]})]});
            var Q10;
            {var subQ0=sQuery(id+"F0.wireOp",EDGE,"E1");var subQ2=sQuery(id+"F0.wireOp",EDGE,"E13");var subQ4=makeQuery(id+"F3.opExtrude","SWEPT_FACE",FACE,{"disambiguationData":[OSD([sQuery(id+"F2.wireOp",EDGE,"E16.MirrorCS")])]});Q10=makeQuery(id+"Fq1PH19bnDTYdRj_1.1.F3.boolean.opBoolean","SPLIT",EDGE,{"disambiguationData":[TD([makeQuery(id+"F3.boolean.opBoolean","COPY",FACE,{"disambiguationData":[OD(0.0)],"derivedFrom":subQ4})])],"derivedFrom":makeQuery(id+"F3.boolean.opBoolean","SPLIT",EDGE,{"disambiguationData":[TD([subQ4])],"derivedFrom":makeQuery(id+"F1.opRevolve","SWEPT_EDGE",EDGE,{"disambiguationData":[OSD([subQ0,subQ2])]})})});}
            var Q11;
            Q11=makeQuery(id+"Fq1PH19bnDTYdRj_1.1.F3.boolean.opBoolean","INTERSECT",EDGE,{"disambiguationData":[OD(0.0)],"derivedFrom":[makeQuery(id+"F1.opRevolve","SWEPT_FACE",FACE,{"disambiguationData":[OSD([sQuery(id+"F0.wireOp",EDGE,"E1")])]}),makeQuery(id+"Fq1PH19bnDTYdRj_1.1.F3.opExtrude","SWEPT_FACE",FACE,{"disambiguationData":[OSD([sQuery(id+"F2.wireOp",EDGE,"E16.MirrorCS")])]})]});
            var Q12;
            Q12=makeQuery(id+"Fq1PH19bnDTYdRj_1.2.F3.boolean.opBoolean","INTERSECT",EDGE,{"disambiguationData":[OD(0.0)],"derivedFrom":[makeQuery(id+"F1.opRevolve","SWEPT_FACE",FACE,{"disambiguationData":[OSD([sQuery(id+"F0.wireOp",EDGE,"E1")])]}),makeQuery(id+"Fq1PH19bnDTYdRj_1.2.F3.opExtrude","SWEPT_FACE",FACE,{"disambiguationData":[OSD([sQuery(id+"F2.wireOp",EDGE,"E15")])]})]});
            var Q13;
            Q13=makeQuery(id+"Fq1PH19bnDTYdRj_1.2.F3.boolean.opBoolean","INTERSECT",EDGE,{"disambiguationData":[OD(0.0)],"derivedFrom":[makeQuery(id+"F1.opRevolve","SWEPT_FACE",FACE,{"disambiguationData":[OSD([sQuery(id+"F0.wireOp",EDGE,"E1")])]}),makeQuery(id+"Fq1PH19bnDTYdRj_1.2.F3.opExtrude","SWEPT_FACE",FACE,{"disambiguationData":[OSD([sQuery(id+"F2.wireOp",EDGE,"E16.MirrorCS")])]})]});
            var Q14;
            Q14=makeQuery(id+"Fq1PH19bnDTYdRj_1.3.F3.boolean.opBoolean","INTERSECT",EDGE,{"disambiguationData":[OD(0.0)],"derivedFrom":[makeQuery(id+"F1.opRevolve","SWEPT_FACE",FACE,{"disambiguationData":[OSD([sQuery(id+"F0.wireOp",EDGE,"E1")])]}),makeQuery(id+"Fq1PH19bnDTYdRj_1.3.F3.opExtrude","SWEPT_FACE",FACE,{"disambiguationData":[OSD([sQuery(id+"F2.wireOp",EDGE,"E15")])]})]});
            var Q15;
            {var subQ0=sQuery(id+"F0.wireOp",EDGE,"E1");var subQ2=sQuery(id+"F0.wireOp",EDGE,"E13");var subQ4=sQuery(id+"F2.wireOp",EDGE,"E16.MirrorCS");var subQ5=makeQuery(id+"Fq1PH19bnDTYdRj_1.2.F3.opExtrude","SWEPT_FACE",FACE,{"disambiguationData":[OSD([subQ4])]});var subQ6=makeQuery(id+"F3.opExtrude","SWEPT_FACE",FACE,{"disambiguationData":[OSD([subQ4])]});var subQ7=makeQuery(id+"F3.boolean.opBoolean","COPY",FACE,{"disambiguationData":[OD(1.0)],"derivedFrom":subQ6});Q15=makeQuery(id+"Fq1PH19bnDTYdRj_1.3.F3.boolean.opBoolean","SPLIT",EDGE,{"disambiguationData":[TD([makeQuery(id+"Fq1PH19bnDTYdRj_1.2.F3.boolean.opBoolean","COPY",FACE,{"disambiguationData":[OD(0.0)],"derivedFrom":subQ5})])],"derivedFrom":makeQuery(id+"Fq1PH19bnDTYdRj_1.2.F3.boolean.opBoolean","SPLIT",EDGE,{"disambiguationData":[TD([subQ7])],"derivedFrom":makeQuery(id+"Fq1PH19bnDTYdRj_1.1.F3.boolean.opBoolean","SPLIT",EDGE,{"disambiguationData":[TD([subQ7])],"derivedFrom":makeQuery(id+"F3.boolean.opBoolean","SPLIT",EDGE,{"disambiguationData":[TD([subQ6])],"derivedFrom":makeQuery(id+"F1.opRevolve","SWEPT_EDGE",EDGE,{"disambiguationData":[OSD([subQ0,subQ2])]})})})})});}
            var Q16;
            {var subQ0=sQuery(id+"F0.wireOp",EDGE,"E1");var subQ2=sQuery(id+"F0.wireOp",EDGE,"E13");var subQ4=sQuery(id+"F2.wireOp",EDGE,"E16.MirrorCS");var subQ5=makeQuery(id+"Fq1PH19bnDTYdRj_1.1.F3.opExtrude","SWEPT_FACE",FACE,{"disambiguationData":[OSD([subQ4])]});var subQ6=makeQuery(id+"F3.opExtrude","SWEPT_FACE",FACE,{"disambiguationData":[OSD([subQ4])]});Q16=makeQuery(id+"Fq1PH19bnDTYdRj_1.2.F3.boolean.opBoolean","SPLIT",EDGE,{"disambiguationData":[TD([makeQuery(id+"Fq1PH19bnDTYdRj_1.1.F3.boolean.opBoolean","COPY",FACE,{"disambiguationData":[OD(0.0)],"derivedFrom":subQ5})])],"derivedFrom":makeQuery(id+"Fq1PH19bnDTYdRj_1.1.F3.boolean.opBoolean","SPLIT",EDGE,{"disambiguationData":[TD([makeQuery(id+"F3.boolean.opBoolean","COPY",FACE,{"disambiguationData":[OD(1.0)],"derivedFrom":subQ6})])],"derivedFrom":makeQuery(id+"F3.boolean.opBoolean","SPLIT",EDGE,{"disambiguationData":[TD([subQ6])],"derivedFrom":makeQuery(id+"F1.opRevolve","SWEPT_EDGE",EDGE,{"disambiguationData":[OSD([subQ0,subQ2])]})})})});}
            var Q17;
            Q17=makeQuery(id+"Fq1PH19bnDTYdRj_1.3.F3.boolean.opBoolean","INTERSECT",EDGE,{"disambiguationData":[OD(0.0)],"derivedFrom":[makeQuery(id+"F1.opRevolve","SWEPT_FACE",FACE,{"disambiguationData":[OSD([sQuery(id+"F0.wireOp",EDGE,"E1")])]}),makeQuery(id+"Fq1PH19bnDTYdRj_1.3.F3.opExtrude","SWEPT_FACE",FACE,{"disambiguationData":[OSD([sQuery(id+"F2.wireOp",EDGE,"E16.MirrorCS")])]})]});
            var Q18;
            Q18=makeQuery(id+"F3.boolean.opBoolean","INTERSECT",EDGE,{"disambiguationData":[OD(1.0)],"derivedFrom":[makeQuery(id+"F1.opRevolve","SWEPT_FACE",FACE,{"disambiguationData":[OSD([sQuery(id+"F0.wireOp",EDGE,"E1")])]}),makeQuery(id+"F3.opExtrude","SWEPT_FACE",FACE,{"disambiguationData":[OSD([sQuery(id+"F2.wireOp",EDGE,"E16.MirrorCS")])]})]});
            var Q19;
            Q19=makeQuery(id+"F3.boolean.opBoolean","INTERSECT",EDGE,{"disambiguationData":[OD(1.0)],"derivedFrom":[makeQuery(id+"F1.opRevolve","SWEPT_FACE",FACE,{"disambiguationData":[OSD([sQuery(id+"F0.wireOp",EDGE,"E1")])]}),makeQuery(id+"F3.opExtrude","SWEPT_FACE",FACE,{"disambiguationData":[OSD([sQuery(id+"F2.wireOp",EDGE,"E15")])]})]});
            var Q20;
            {var subQ0=sQuery(id+"F0.wireOp",EDGE,"E1");var subQ2=sQuery(id+"F2.wireOp",EDGE,"E16.MirrorCS");var subQ3=sQuery(id+"F0.wireOp",EDGE,"E13");var subQ5=makeQuery(id+"F3.opExtrude","SWEPT_FACE",FACE,{"disambiguationData":[OSD([subQ2])]});var subQ6=makeQuery(id+"F3.boolean.opBoolean","COPY",FACE,{"disambiguationData":[OD(1.0)],"derivedFrom":subQ5});Q20=makeQuery(id+"Fq1PH19bnDTYdRj_1.3.F3.boolean.opBoolean","SPLIT",EDGE,{"disambiguationData":[TD([subQ6])],"derivedFrom":makeQuery(id+"Fq1PH19bnDTYdRj_1.2.F3.boolean.opBoolean","SPLIT",EDGE,{"disambiguationData":[TD([subQ6])],"derivedFrom":makeQuery(id+"Fq1PH19bnDTYdRj_1.1.F3.boolean.opBoolean","SPLIT",EDGE,{"disambiguationData":[TD([subQ6])],"derivedFrom":makeQuery(id+"F3.boolean.opBoolean","SPLIT",EDGE,{"disambiguationData":[TD([subQ5])],"derivedFrom":makeQuery(id+"F1.opRevolve","SWEPT_EDGE",EDGE,{"disambiguationData":[OSD([subQ0,subQ3])]})})})})});}
            var Q21;
            {var subQ0=sQuery(id+"F0.wireOp",EDGE,"E1");var subQ2=sQuery(id+"F0.wireOp",EDGE,"E13");var subQ4=makeQuery(id+"F3.opExtrude","SWEPT_FACE",FACE,{"disambiguationData":[OSD([sQuery(id+"F2.wireOp",EDGE,"E15")])]});Q21=makeQuery(id+"Fq1PH19bnDTYdRj_1.1.F3.boolean.opBoolean","SPLIT",EDGE,{"disambiguationData":[TD([makeQuery(id+"F3.boolean.opBoolean","COPY",FACE,{"disambiguationData":[OD(1.0)],"derivedFrom":subQ4})])],"derivedFrom":makeQuery(id+"F3.boolean.opBoolean","SPLIT",EDGE,{"disambiguationData":[TD([subQ4])],"derivedFrom":makeQuery(id+"F1.opRevolve","SWEPT_EDGE",EDGE,{"disambiguationData":[OSD([subQ0,subQ2])]})})});}
            var Q22;
            Q22=makeQuery(id+"Fq1PH19bnDTYdRj_1.1.F3.boolean.opBoolean","INTERSECT",EDGE,{"disambiguationData":[OD(1.0)],"derivedFrom":[makeQuery(id+"F1.opRevolve","SWEPT_FACE",FACE,{"disambiguationData":[OSD([sQuery(id+"F0.wireOp",EDGE,"E1")])]}),makeQuery(id+"Fq1PH19bnDTYdRj_1.1.F3.opExtrude","SWEPT_FACE",FACE,{"disambiguationData":[OSD([sQuery(id+"F2.wireOp",EDGE,"E16.MirrorCS")])]})]});
            var Q23;
            Q23=makeQuery(id+"Fq1PH19bnDTYdRj_1.1.F3.boolean.opBoolean","INTERSECT",EDGE,{"disambiguationData":[OD(1.0)],"derivedFrom":[makeQuery(id+"F1.opRevolve","SWEPT_FACE",FACE,{"disambiguationData":[OSD([sQuery(id+"F0.wireOp",EDGE,"E1")])]}),makeQuery(id+"Fq1PH19bnDTYdRj_1.1.F3.opExtrude","SWEPT_FACE",FACE,{"disambiguationData":[OSD([sQuery(id+"F2.wireOp",EDGE,"E15")])]})]});
            fillet(context, id + "F12", {"entities" : qUnion([Q0, Q1, Q2, Q3, Q4, Q5, Q6, Q7, Q8, Q9, Q10, Q11, Q12, Q13, Q14, Q15, Q16, Q17, Q18, Q19, Q20, Q21, Q22, Q23]), "radius" : 1 * mm, "tangentPropagation" : true, "allowEdgeOverflow" : false});
        }
    });
